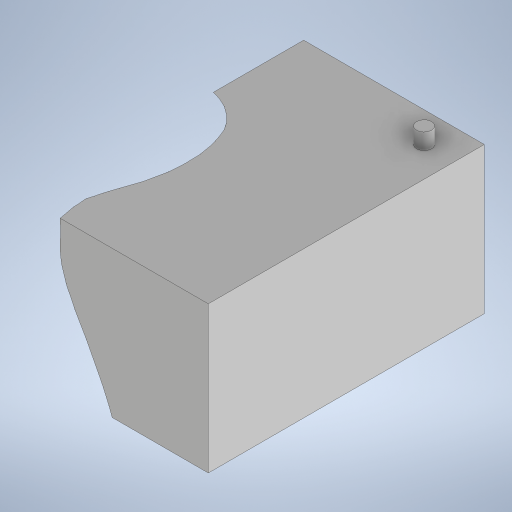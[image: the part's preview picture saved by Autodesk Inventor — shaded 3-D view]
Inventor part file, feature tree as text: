
AUTODESK INVENTOR PART (.ipt)
format: ipt  version: 2024 (Build 280153000, 153)  size: 10,762,240 bytes
history: native  units: mm
features: other x6, extrude x6, sketch x6, plane x2
ambient origin geometry x8: Origin, YZ Plane, XZ Plane, XY Plane, X Axis, Y Axis, Z Axis, Center Point
bodies: Body1 (feature_tree)
feature tree (20):
  other  "M.ipt"
  plane  "Plano de trabajo1"
  extrude  "Extrusión1"  [1 undecoded]
  other  "Combinar1"
  sketch  "Boceto3"  dims[d2=550.0mm d3=520.0mm]
  sketch  "Boceto4"  dims[d4=550.0mm d5=0.0mm d6=129.8482mm]
  plane  "Plano de trabajo2"
  sketch  "Boceto5"  dims[d17=180.0mm d18=180.0mm]
  extrude  "Extrusión2"  Depth=520.0mm
  extrude  "Extrusión3"  Depth=129.8482mm
  extrude  "Extrusión4"  Depth=180.0mm
  extrude  "Extrusión5"  Depth=180.0mm
  extrude  "Extrusión6"  Depth=180.0mm
  other  "Sólido1::M.ipt"
  other  "OperaciónIdentificador1"
  sketch  "Boceto1"  dims[d0=25.0mm d1=-365.0mm]
  other  "Sólido2"
  sketch  "Boceto6"  dims[d22=326.0mm d23=180.0mm]
  sketch  "Boceto7"  dims[d24=180.0mm d25=180.0mm d26=10.0mm d27=0.0mm d28=1000.0mm d29=0.0mm d30=1000.0mm d31=0.0mm d32=30.0mm d33=30.0mm d34=16.0mm d35=16.0mm d36=0.0mm d37=30.0mm d38=30.0mm d39=15.0mm d40=16.0mm d41=161.0mm d42=0.0mm d43=0.0mm d14=0.5mm d15=0.872665mm d16=0.5mm d19=0.5mm d20=0.872665mm d21=0.5mm]
  other  "Sólido1"
note: 1 required parameter value undecoded (feature->parameter linkage not recoverable at this tier; creation-order binding heuristic only, values carry confidence <= 0.55)
